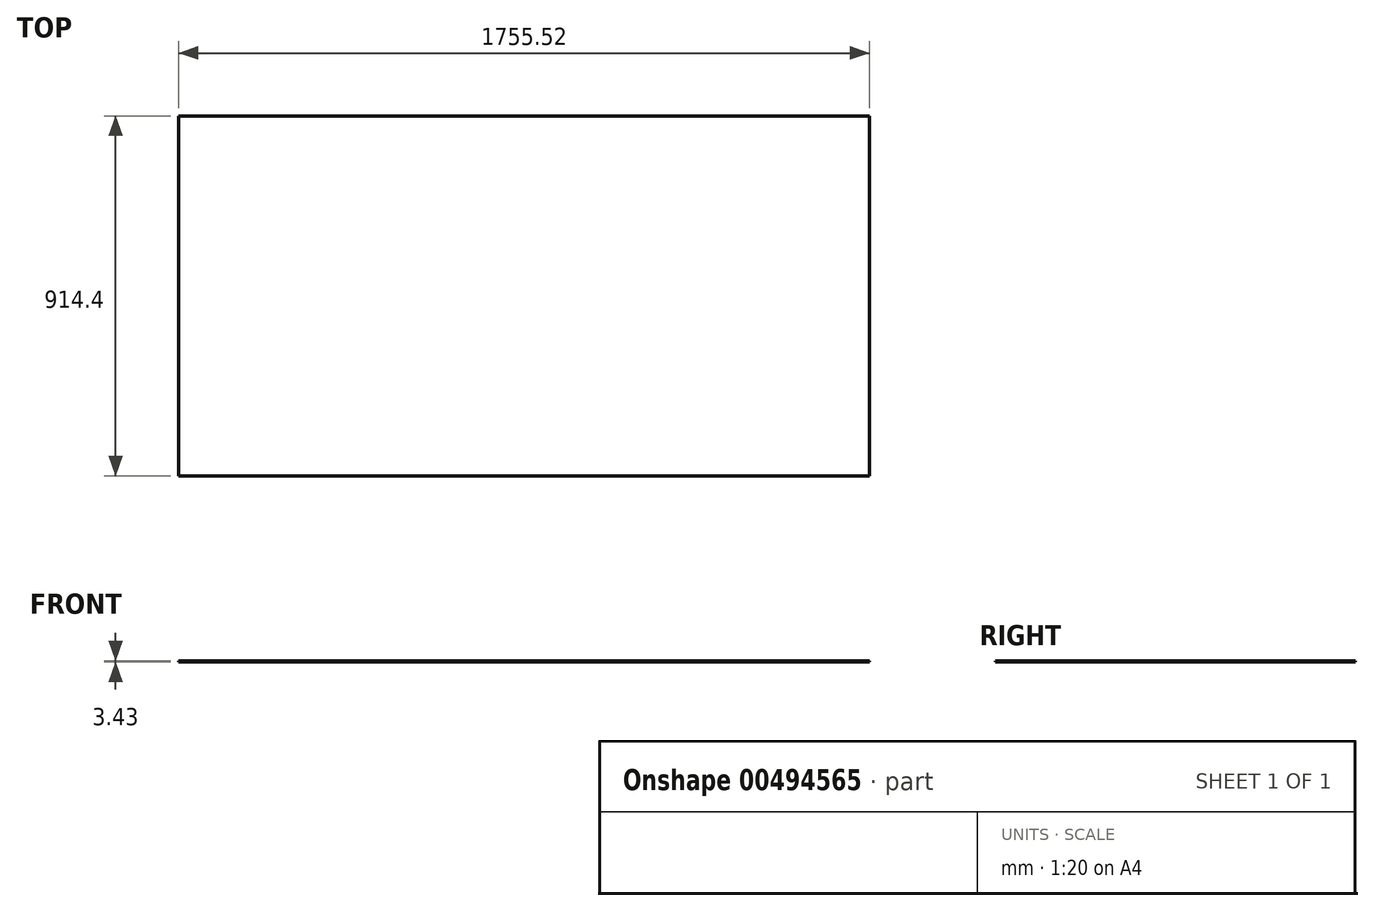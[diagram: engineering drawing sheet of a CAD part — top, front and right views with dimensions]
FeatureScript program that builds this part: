
annotation { "Feature Type Name" : "Feature", "Feature Type Description" : "" }
export const myFeature = defineFeature(function(context is Context, id is Id, definition is map)
    precondition{}
    {
        {
            var Q0;
            Q0=qCreatedBy(makeId("Top.planeOp"),FACE);
            var sketch = newSketch(context, id + "F0", { "sketchPlane" : qUnion([Q0])});
            skLineSegment(sketch, "E0.bottom", {"start": v(0, 0) * mm, "end": v(1755.52, 0) * mm});
            skLineSegment(sketch, "E0.top", {"start": v(0, 914.4) * mm, "end": v(1755.52, 914.4) * mm});
            skLineSegment(sketch, "E0.left", {"start": v(0, 0) * mm, "end": v(0, 914.4) * mm});
            skLineSegment(sketch, "E0.right", {"start": v(1755.52, 0) * mm, "end": v(1755.52, 914.4) * mm});
            skSolve(sketch);
        }
        {
            var Q0;
            Q0=makeQuery(id+"F0.imprint","IMPRINT",FACE,{"disambiguationData":[TD([[makeQuery(id+"F0.imprint","IMPRINT",EDGE,{"derivedFrom":sQuery(id+"F0.wireOp",EDGE,"E0.bottom")}),1.0]])]});
            extrude(context, id + "F1", {"entities" : qUnion([Q0]), "depth" : 3.43 * mm});
        }
    });
